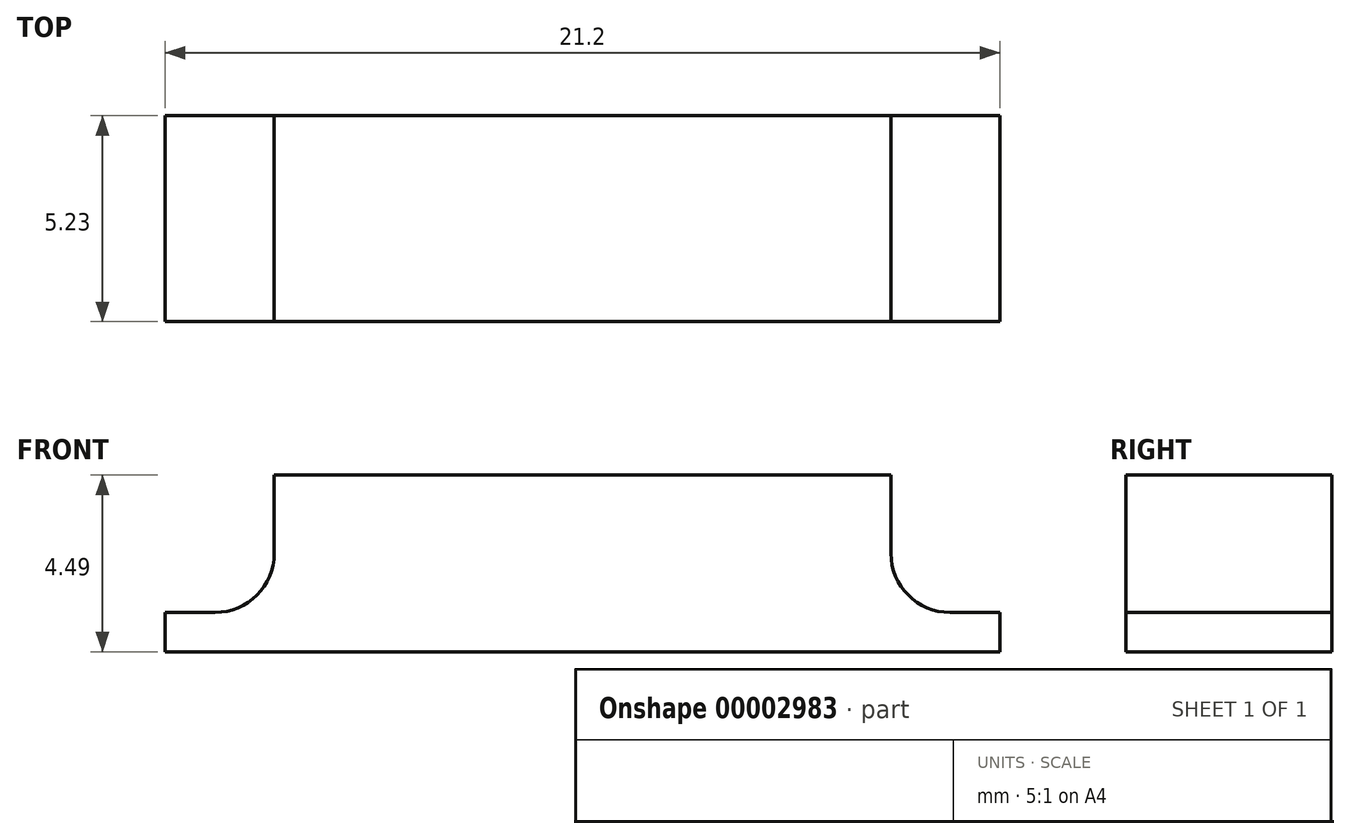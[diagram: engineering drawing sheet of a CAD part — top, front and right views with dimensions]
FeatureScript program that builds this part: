
annotation { "Feature Type Name" : "Feature", "Feature Type Description" : "" }
export const myFeature = defineFeature(function(context is Context, id is Id, definition is map)
    precondition{}
    {
        {
            var Q0;
            Q0=qCreatedBy(makeId("Front.planeOp"),FACE);
            var sketch = newSketch(context, id + "F0", { "sketchPlane" : qUnion([Q0])});
            skLineSegment(sketch, "E0", {"start": v(0, 10.25) * mm, "end": v(0, -11.27) * mm, "construction": true});
            skLineSegment(sketch, "E1", {"start": v(0, 0.66) * mm, "end": v(-7.84, 0.66) * mm});
            skLineSegment(sketch, "E2.0.MirrorCS", {"start": v(0, 0.66) * mm, "end": v(7.84, 0.66) * mm});
            skLineSegment(sketch, "E3", {"start": v(-7.84, 0.66) * mm, "end": v(-7.84, -1.33) * mm});
            skLineSegment(sketch, "E4", {"start": v(-9.34, -2.83) * mm, "end": v(-10.6, -2.83) * mm});
            skLineSegment(sketch, "E5", {"start": v(-10.6, -2.83) * mm, "end": v(-10.6, -3.83) * mm});
            skLineSegment(sketch, "E6", {"start": v(-10.6, -3.83) * mm, "end": v(0, -3.83) * mm});
            skLineSegment(sketch, "E7.0.MirrorCS", {"start": v(10.6, -3.83) * mm, "end": v(0, -3.83) * mm});
            skLineSegment(sketch, "E8.0.MirrorCS", {"start": v(9.34, -2.83) * mm, "end": v(10.6, -2.83) * mm});
            skLineSegment(sketch, "E8.1.MirrorCS", {"start": v(7.84, 0.66) * mm, "end": v(7.84, -1.33) * mm});
            skLineSegment(sketch, "E9.0.MirrorCS", {"start": v(10.6, -2.83) * mm, "end": v(10.6, -3.83) * mm});
            skPoint(sketch, "E10.visualSharp", {"position": v(-7.84, -2.83) * mm});
            skArc(sketch, "E10.filletArc", {"start": v(-9.34, -2.83) * mm, "mid": v(-8.27, -2.4) * mm, "end": v(-7.84, -1.33) * mm});
            skPoint(sketch, "E11.visualSharp", {"position": v(7.84, -2.83) * mm});
            skArc(sketch, "E11.filletArc", {"start": v(7.84, -1.33) * mm, "mid": v(8.27, -2.4) * mm, "end": v(9.34, -2.83) * mm});
            skSolve(sketch);
        }
        {
            var Q0;
            Q0 = qSketchRegion(id + "F0", true);
            extrude(context, id + "F1", {"entities" : qUnion([Q0]), "depth" : 5.23 * mm});
        }
    });
